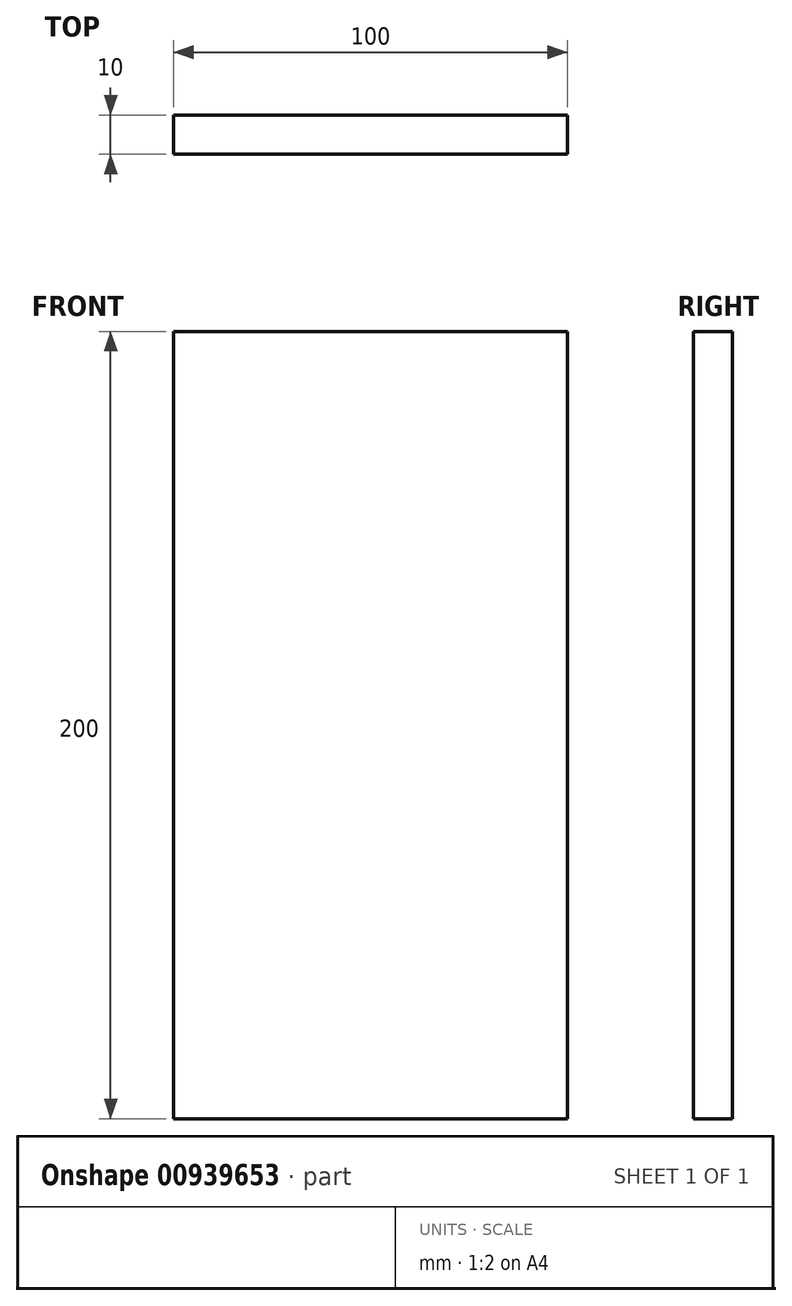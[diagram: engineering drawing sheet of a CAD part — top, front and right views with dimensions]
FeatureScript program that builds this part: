
annotation { "Feature Type Name" : "Feature", "Feature Type Description" : "" }
export const myFeature = defineFeature(function(context is Context, id is Id, definition is map)
    precondition{}
    {
        {
            var Q0;
            Q0=qCreatedBy(makeId("Front.planeOp"),FACE);
            var sketch = newSketch(context, id + "F0", { "sketchPlane" : qUnion([Q0])});
            skLineSegment(sketch, "E0.bottom", {"start": v(50, -100) * mm, "end": v(-50, -100) * mm});
            skLineSegment(sketch, "E0.top", {"start": v(50, 100) * mm, "end": v(-50, 100) * mm});
            skLineSegment(sketch, "E0.left", {"start": v(50, -100) * mm, "end": v(50, 100) * mm});
            skLineSegment(sketch, "E0.right", {"start": v(-50, -100) * mm, "end": v(-50, 100) * mm});
            skPoint(sketch, "E0.middle", {"position": v(0, 0) * mm});
            skSolve(sketch);
        }
        {
            var Q0;
            Q0 = qSketchRegion(id + "F0", true);
            extrude(context, id + "F1", {"entities" : qUnion([Q0]), "oppositeDirection" : true, "depth" : 10 * mm, "offsetDistance" : 25 * mm});
        }
    });
